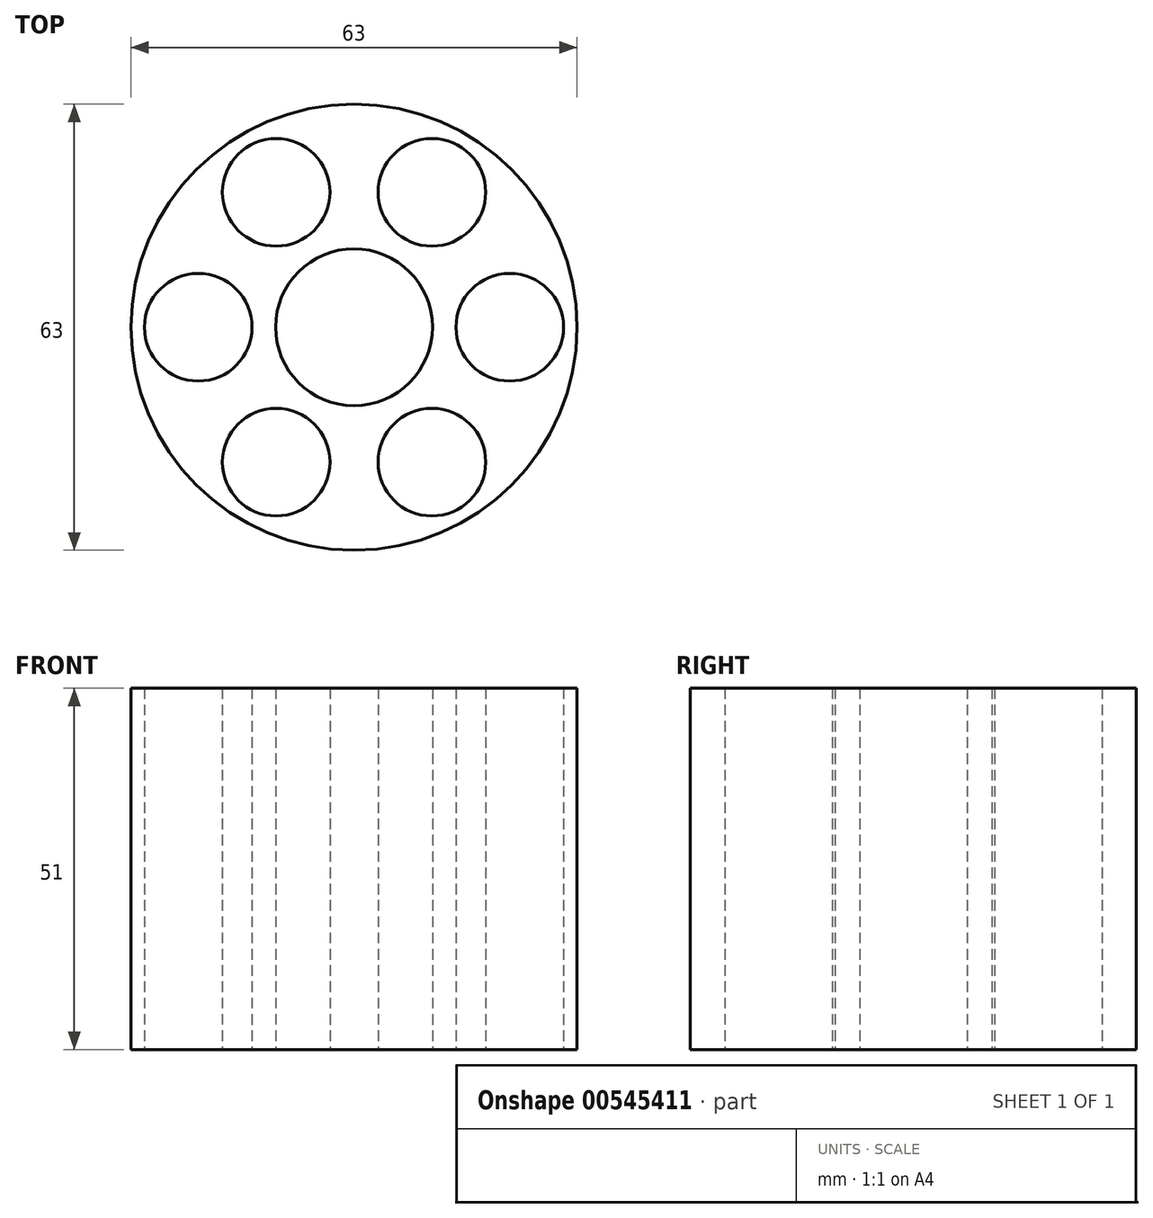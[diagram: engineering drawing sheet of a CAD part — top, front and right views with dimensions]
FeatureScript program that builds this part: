
annotation { "Feature Type Name" : "Feature", "Feature Type Description" : "" }
export const myFeature = defineFeature(function(context is Context, id is Id, definition is map)
    precondition{}
    {
        {
            var Q0;
            Q0=qCreatedBy(makeId("Top.planeOp"),FACE);
            var sketch = newSketch(context, id + "F0", { "sketchPlane" : qUnion([Q0])});
            skCircle(sketch, "E0", {"center": v(0, 0) * mm, "radius": 11.07 * mm});
            skLineSegment(sketch, "E1", {"start": v(0, 0) * mm, "end": v(22, 0) * mm});
            skCircle(sketch, "E2", {"center": v(22, 0) * mm, "radius": 7.6 * mm});
            skLineSegment(sketch, "E3", {"start": v(0, 0) * mm, "end": v(11, 19.05) * mm});
            skCircle(sketch, "E4", {"center": v(11, 19.05) * mm, "radius": 7.6 * mm});
            skLineSegment(sketch, "E5", {"start": v(0, 0) * mm, "end": v(-11, 19.05) * mm});
            skCircle(sketch, "E6", {"center": v(-11, 19.05) * mm, "radius": 7.6 * mm});
            skLineSegment(sketch, "E7", {"start": v(0, 0) * mm, "end": v(-22, 0) * mm});
            skCircle(sketch, "E8", {"center": v(-22, 0) * mm, "radius": 7.6 * mm});
            skLineSegment(sketch, "E9", {"start": v(0, 0) * mm, "end": v(11, -19.05) * mm});
            skCircle(sketch, "E10", {"center": v(11, -19.05) * mm, "radius": 7.6 * mm});
            skLineSegment(sketch, "E11", {"start": v(0, 0) * mm, "end": v(-11, -19.05) * mm});
            skCircle(sketch, "E12", {"center": v(-11, -19.05) * mm, "radius": 7.6 * mm});
            skCircle(sketch, "E13", {"center": v(0, 0) * mm, "radius": 31.5 * mm});
            skSolve(sketch);
        }
        {
            var Q0;
            Q0=makeQuery(id+"F0.imprint","IMPRINT",FACE,{"disambiguationData":[TD([[makeQuery(id+"F0.imprint","IMPRINT",EDGE,{"derivedFrom":sQuery(id+"F0.wireOp",EDGE,"E2")}),-1.0]])]});
            extrude(context, id + "F1", {"entities" : qUnion([Q0]), "depth" : 51 * mm, "offsetDistance" : 25 * mm});
        }
    });
